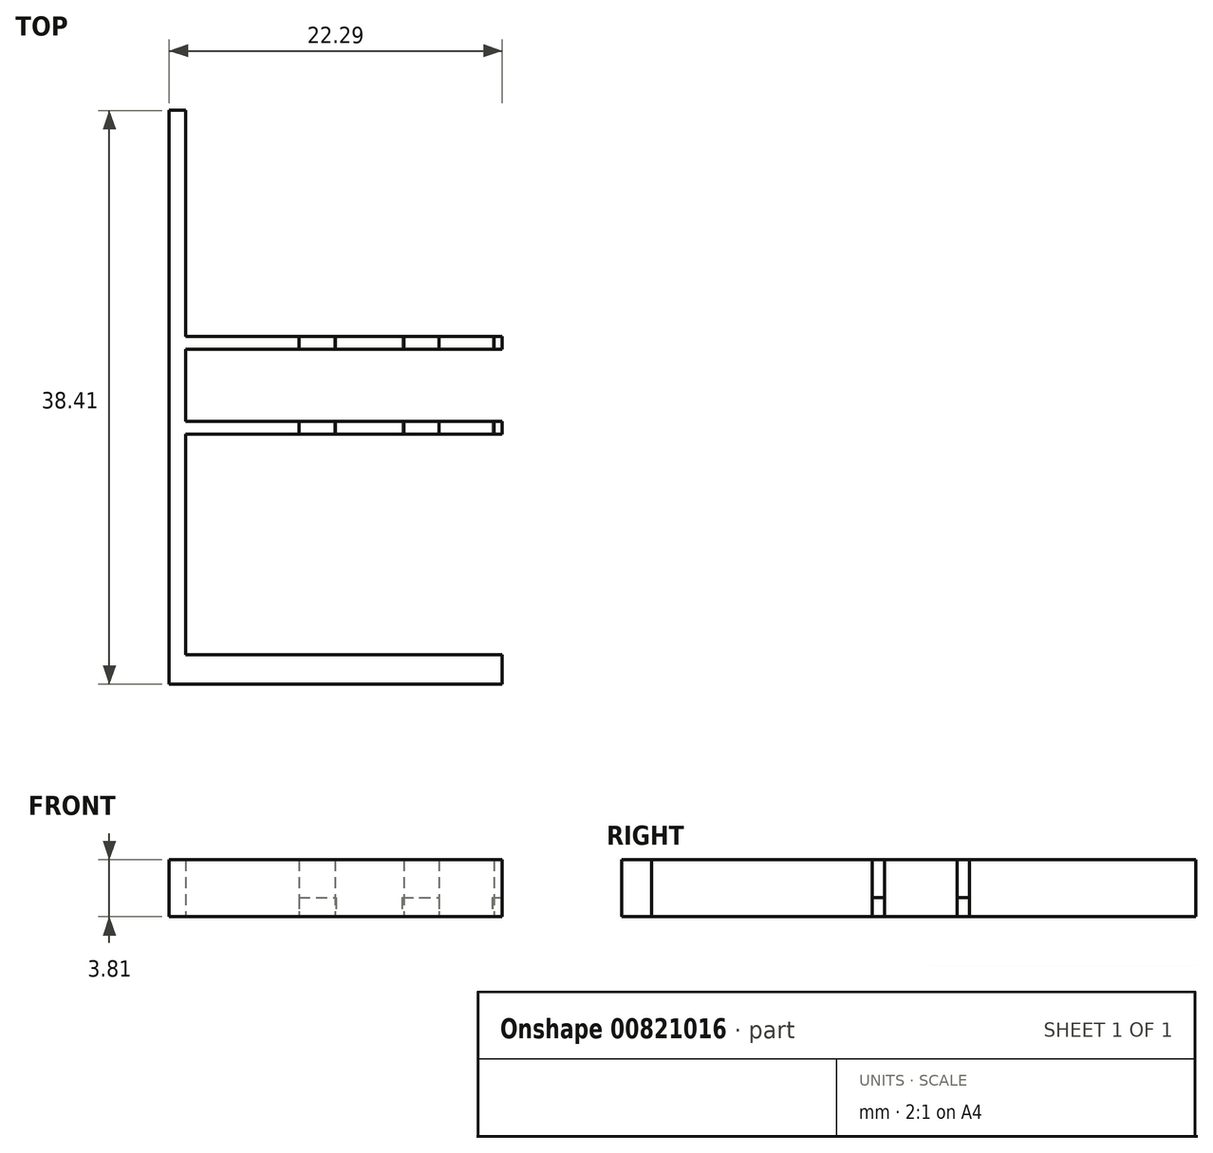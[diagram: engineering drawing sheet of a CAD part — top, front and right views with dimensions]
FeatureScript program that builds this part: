
annotation { "Feature Type Name" : "Feature", "Feature Type Description" : "" }
export const myFeature = defineFeature(function(context is Context, id is Id, definition is map)
    precondition{}
    {
        {
            var Q0;
            Q0=qCreatedBy(makeId("Top.planeOp"),FACE);
            var sketch = newSketch(context, id + "F0", { "sketchPlane" : qUnion([Q0])});
            skLineSegment(sketch, "E0.bottom", {"start": v(-77.22, -52.84) * mm, "end": v(-68.58, -52.84) * mm});
            skLineSegment(sketch, "E0.top", {"start": v(-77.22, -53.68) * mm, "end": v(-68.58, -53.68) * mm});
            skLineSegment(sketch, "E0.left", {"start": v(-77.22, -52.84) * mm, "end": v(-77.22, -53.68) * mm});
            skLineSegment(sketch, "E0.right", {"start": v(-68.58, -52.84) * mm, "end": v(-68.58, -53.68) * mm});
            skLineSegment(sketch, "E1.bottom", {"start": v(-77.22, -59.37) * mm, "end": v(-68.58, -59.37) * mm});
            skLineSegment(sketch, "E1.top", {"start": v(-77.22, -58.53) * mm, "end": v(-68.58, -58.53) * mm});
            skLineSegment(sketch, "E1.left", {"start": v(-77.22, -59.37) * mm, "end": v(-77.22, -58.53) * mm});
            skLineSegment(sketch, "E1.right", {"start": v(-68.58, -59.37) * mm, "end": v(-68.58, -58.53) * mm});
            skLineSegment(sketch, "E2.bottom", {"start": v(-66.17, -53.68) * mm, "end": v(-61.55, -53.68) * mm});
            skLineSegment(sketch, "E2.top", {"start": v(-66.17, -52.84) * mm, "end": v(-61.55, -52.84) * mm});
            skLineSegment(sketch, "E2.left", {"start": v(-66.17, -53.68) * mm, "end": v(-66.17, -52.84) * mm});
            skLineSegment(sketch, "E2.right", {"start": v(-61.55, -53.68) * mm, "end": v(-61.55, -52.84) * mm});
            skLineSegment(sketch, "E3.bottom", {"start": v(-66.17, -58.53) * mm, "end": v(-61.55, -58.53) * mm});
            skLineSegment(sketch, "E3.top", {"start": v(-66.17, -59.37) * mm, "end": v(-61.55, -59.37) * mm});
            skLineSegment(sketch, "E3.left", {"start": v(-66.17, -58.53) * mm, "end": v(-66.17, -59.37) * mm});
            skLineSegment(sketch, "E3.right", {"start": v(-61.55, -58.53) * mm, "end": v(-61.55, -59.37) * mm});
            skLineSegment(sketch, "E4.bottom", {"start": v(-55.53, -59.37) * mm, "end": v(-59.21, -59.37) * mm});
            skLineSegment(sketch, "E4.top", {"start": v(-55.53, -58.53) * mm, "end": v(-59.21, -58.53) * mm});
            skLineSegment(sketch, "E4.left", {"start": v(-55.53, -59.37) * mm, "end": v(-55.53, -58.53) * mm});
            skLineSegment(sketch, "E4.right", {"start": v(-59.21, -59.37) * mm, "end": v(-59.21, -58.53) * mm});
            skLineSegment(sketch, "E5.bottom", {"start": v(-59.21, -52.84) * mm, "end": v(-55.53, -52.84) * mm});
            skLineSegment(sketch, "E5.top", {"start": v(-59.21, -53.68) * mm, "end": v(-55.53, -53.68) * mm});
            skLineSegment(sketch, "E5.left", {"start": v(-59.21, -52.84) * mm, "end": v(-59.21, -53.68) * mm});
            skLineSegment(sketch, "E5.right", {"start": v(-55.53, -52.84) * mm, "end": v(-55.53, -53.68) * mm});
            skLineSegment(sketch, "E6.top", {"start": v(-77.26, -76.11) * mm, "end": v(-76.15, -76.11) * mm});
            skLineSegment(sketch, "E6.left", {"start": v(-77.26, -37.7) * mm, "end": v(-77.26, -76.11) * mm});
            skLineSegment(sketch, "E6.right", {"start": v(-76.15, -37.7) * mm, "end": v(-76.15, -76.11) * mm});
            skLineSegment(sketch, "E7.bottom", {"start": v(-77.26, -76.11) * mm, "end": v(-54.98, -76.11) * mm});
            skLineSegment(sketch, "E7.top", {"start": v(-77.26, -74.13) * mm, "end": v(-54.98, -74.13) * mm});
            skLineSegment(sketch, "E7.left", {"start": v(-77.26, -76.11) * mm, "end": v(-77.26, -74.13) * mm});
            skLineSegment(sketch, "E7.right", {"start": v(-54.98, -76.11) * mm, "end": v(-54.98, -74.13) * mm});
            skLineSegment(sketch, "E8", {"start": v(-76.15, -37.7) * mm, "end": v(-77.26, -37.7) * mm});
            skSolve(sketch);
        }
        {
            var Q0;
            Q0 = qSketchRegion(id + "F0", true);
            extrude(context, id + "F1", {"entities" : qUnion([Q0]), "depth" : 3.8 * mm, "offsetDistance" : 25.4 * mm});
        }
        {
            var Q0;
            Q0=qCreatedBy(makeId("Top.planeOp"),FACE);
            var sketch = newSketch(context, id + "F2", { "sketchPlane" : qUnion([Q0])});
            skLineSegment(sketch, "E9.bottom", {"start": v(-68.58, -52.84) * mm, "end": v(-66.1, -52.84) * mm});
            skLineSegment(sketch, "E9.top", {"start": v(-68.58, -53.68) * mm, "end": v(-66.1, -53.68) * mm});
            skLineSegment(sketch, "E9.left", {"start": v(-68.58, -52.84) * mm, "end": v(-68.58, -53.68) * mm});
            skLineSegment(sketch, "E9.right", {"start": v(-66.1, -52.84) * mm, "end": v(-66.1, -53.68) * mm});
            skLineSegment(sketch, "E10.bottom", {"start": v(-68.58, -58.53) * mm, "end": v(-66.1, -58.53) * mm});
            skLineSegment(sketch, "E10.top", {"start": v(-68.58, -59.37) * mm, "end": v(-66.1, -59.37) * mm});
            skLineSegment(sketch, "E10.left", {"start": v(-68.58, -58.53) * mm, "end": v(-68.58, -59.37) * mm});
            skLineSegment(sketch, "E10.right", {"start": v(-66.1, -58.53) * mm, "end": v(-66.1, -59.37) * mm});
            skLineSegment(sketch, "E11.bottom", {"start": v(-61.68, -52.84) * mm, "end": v(-59.21, -52.84) * mm});
            skLineSegment(sketch, "E11.top", {"start": v(-61.68, -53.68) * mm, "end": v(-59.21, -53.68) * mm});
            skLineSegment(sketch, "E11.left", {"start": v(-61.68, -52.84) * mm, "end": v(-61.68, -53.68) * mm});
            skLineSegment(sketch, "E11.right", {"start": v(-59.21, -52.84) * mm, "end": v(-59.21, -53.68) * mm});
            skLineSegment(sketch, "E12.bottom", {"start": v(-61.68, -58.53) * mm, "end": v(-59.21, -58.53) * mm});
            skLineSegment(sketch, "E12.top", {"start": v(-61.68, -59.37) * mm, "end": v(-59.21, -59.37) * mm});
            skLineSegment(sketch, "E12.left", {"start": v(-61.68, -58.53) * mm, "end": v(-61.68, -59.37) * mm});
            skLineSegment(sketch, "E12.right", {"start": v(-59.21, -58.53) * mm, "end": v(-59.21, -59.37) * mm});
            skLineSegment(sketch, "E13.bottom", {"start": v(-55.6, -52.84) * mm, "end": v(-54.97, -52.84) * mm});
            skLineSegment(sketch, "E13.top", {"start": v(-55.6, -53.68) * mm, "end": v(-54.97, -53.68) * mm});
            skLineSegment(sketch, "E13.left", {"start": v(-55.6, -52.84) * mm, "end": v(-55.6, -53.68) * mm});
            skLineSegment(sketch, "E13.right", {"start": v(-54.97, -52.84) * mm, "end": v(-54.97, -53.68) * mm});
            skLineSegment(sketch, "E14.bottom", {"start": v(-55.66, -58.53) * mm, "end": v(-54.97, -58.53) * mm});
            skLineSegment(sketch, "E14.top", {"start": v(-55.66, -59.37) * mm, "end": v(-54.97, -59.37) * mm});
            skLineSegment(sketch, "E14.left", {"start": v(-55.66, -58.53) * mm, "end": v(-55.66, -59.37) * mm});
            skLineSegment(sketch, "E14.right", {"start": v(-54.97, -58.53) * mm, "end": v(-54.97, -59.37) * mm});
            skSolve(sketch);
        }
        {
            var Q0;
            Q0 = qSketchRegion(id + "F2", true);
            extrude(context, id + "F3", {"entities" : qUnion([Q0]), "depth" : 1.27 * mm, "offsetDistance" : 25.4 * mm});
        }
    });
